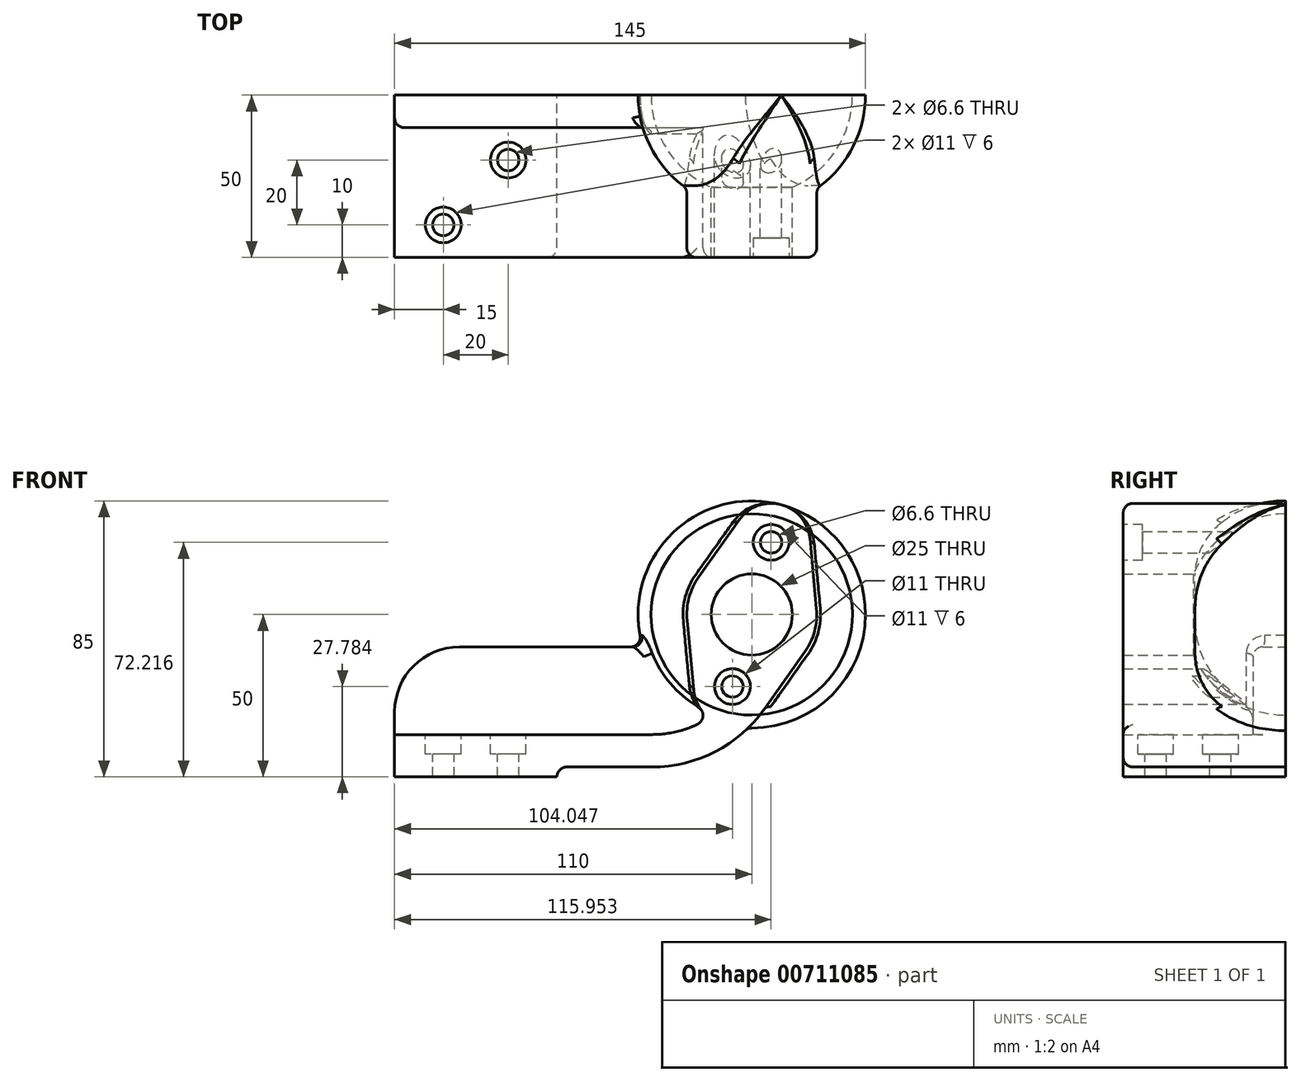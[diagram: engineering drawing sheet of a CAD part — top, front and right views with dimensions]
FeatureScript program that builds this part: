
annotation { "Feature Type Name" : "Feature", "Feature Type Description" : "" }
export const myFeature = defineFeature(function(context is Context, id is Id, definition is map)
    precondition{}
    {
        {
            var Q0;
            Q0=qCreatedBy(makeId("Front.planeOp"),FACE);
            var sketch = newSketch(context, id + "F0", { "sketchPlane" : qUnion([Q0])});
            skCircle(sketch, "E0", {"center": v(0, 0) * mm, "radius": 35 * mm});
            skLineSegment(sketch, "E1", {"start": v(-35, 0) * mm, "end": v(35, 0) * mm});
            skSolve(sketch);
        }
        {
            var Q0;
            {var subQ0=sQuery(id+"F0.wireOp",EDGE,"E1");Q0=makeQuery(id+"F0.imprint","IMPRINT",FACE,{"disambiguationData":[TD([[makeQuery(id+"F0.imprint","IMPRINT",EDGE,{"derivedFrom":subQ0}),1.0]])]});}
            var Q1;
            Q1=sQuery(id+"F0.wireOp",EDGE,"E1");
            revolve(context, id + "F1", {"surfaceOperationType" : NewSurfaceOperationType.NEW, "entities" : qUnion([Q0]), "axis" : qUnion([Q1]), "revolveType" : RevolveType.ONE_DIRECTION, "angle" : 180 * degree});
        }
        {
            var Q0;
            Q0=qCreatedBy(makeId("Front.planeOp"),FACE);
            var sketch = newSketch(context, id + "F2", { "sketchPlane" : qUnion([Q0])});
            skCircle(sketch, "E2.0", {"center": v(0, 0) * mm, "radius": 35 * mm});
            skLineSegment(sketch, "E3", {"start": v(-33.54, -10) * mm, "end": v(-110, -10) * mm});
            skLineSegment(sketch, "E4", {"start": v(-110, -10) * mm, "end": v(-110, -50) * mm});
            skLineSegment(sketch, "E5", {"start": v(-110, -50) * mm, "end": v(-60, -50) * mm});
            skLineSegment(sketch, "E6", {"start": v(-60, -50) * mm, "end": v(-60, -47) * mm});
            skLineSegment(sketch, "E7", {"start": v(-60, -47) * mm, "end": v(-30.7, -47) * mm});
            skArc(sketch, "E8", {"start": v(-30.7, -47) * mm, "mid": v(-11.26, -42.28) * mm, "end": v(3.83, -29.16) * mm});
            skLineSegment(sketch, "E9", {"start": v(-110, -37) * mm, "end": v(-30.7, -37) * mm});
            skArc(sketch, "E10", {"start": v(-30.7, -37) * mm, "mid": v(-21.55, -35.68) * mm, "end": v(-13.14, -31.82) * mm});
            skLineSegment(sketch, "E11", {"start": v(0, 35) * mm, "end": v(0, -35) * mm, "construction": true});
            skLineSegment(sketch, "E12", {"start": v(-35, 0) * mm, "end": v(35, 0) * mm, "construction": true});
            skLineSegment(sketch, "E13", {"start": v(9.06, 33.8) * mm, "end": v(-9.06, -33.8) * mm, "construction": true});
            skLineSegment(sketch, "E14", {"start": v(-33.8, 9.06) * mm, "end": v(33.8, -9.06) * mm, "construction": true});
            skCircle(sketch, "E15", {"center": v(0, 0) * mm, "radius": 12.5 * mm});
            skCircle(sketch, "E16", {"center": v(5.95, 22.22) * mm, "radius": 3.3 * mm});
            skCircle(sketch, "E17", {"center": v(5.95, 22.22) * mm, "radius": 5.5 * mm});
            skCircle(sketch, "E18.MirrorC", {"center": v(-5.95, -22.22) * mm, "radius": 5.5 * mm});
            skCircle(sketch, "E19.MirrorC", {"center": v(-5.95, -22.22) * mm, "radius": 3.3 * mm});
            skCircle(sketch, "E20", {"center": v(0, 0) * mm, "radius": 23 * mm, "construction": true});
            skArc(sketch, "E21", {"start": v(17.9, 23.34) * mm, "mid": v(15.12, 29.96) * mm, "end": v(9.06, 33.8) * mm});
            skArc(sketch, "E22", {"start": v(19.32, -5.18) * mm, "mid": v(19.93, -1.68) * mm, "end": v(19.91, 1.87) * mm});
            skLineSegment(sketch, "E23", {"start": v(17.9, 23.34) * mm, "end": v(19.91, 1.87) * mm});
            skArc(sketch, "E24.MirrorCS", {"start": v(-3.83, 29.16) * mm, "mid": v(1.88, 33.5) * mm, "end": v(9.06, 33.8) * mm});
            skLineSegment(sketch, "E25.MirrorCS", {"start": v(-3.83, 29.16) * mm, "end": v(-16.31, 11.57) * mm});
            skArc(sketch, "E26.MirrorCS", {"start": v(-19.32, 5.18) * mm, "mid": v(-18.1, 8.5) * mm, "end": v(-16.31, 11.57) * mm});
            skArc(sketch, "E27.MirrorCS", {"start": v(-19.32, 5.18) * mm, "mid": v(-19.93, 1.68) * mm, "end": v(-19.91, -1.87) * mm});
            skLineSegment(sketch, "E28.MirrorCS", {"start": v(-17.9, -23.34) * mm, "end": v(-19.91, -1.87) * mm});
            skArc(sketch, "E29.MirrorCS", {"start": v(-17.9, -23.34) * mm, "mid": v(-15.12, -29.96) * mm, "end": v(-9.06, -33.8) * mm});
            skLineSegment(sketch, "E30.MirrorCS", {"start": v(3.83, -29.16) * mm, "end": v(16.31, -11.57) * mm});
            skArc(sketch, "E31.MirrorCS", {"start": v(19.32, -5.18) * mm, "mid": v(18.1, -8.5) * mm, "end": v(16.31, -11.57) * mm});
            skArc(sketch, "E32", {"start": v(-9.06, -33.8) * mm, "mid": v(-1.88, -33.5) * mm, "end": v(3.83, -29.16) * mm});
            skLineSegment(sketch, "E33", {"start": v(-33.54, -10) * mm, "end": v(-13.14, -10) * mm});
            skLineSegment(sketch, "E34", {"start": v(-13.14, -10) * mm, "end": v(-13.14, -31.82) * mm});
            skSolve(sketch);
        }
        {
            var Q0;
            {var subQ0=sQuery(id+"F2.wireOp",EDGE,"E5");Q0=makeQuery(id+"F2.imprint","IMPRINT",FACE,{"disambiguationData":[TD([[makeQuery(id+"F2.imprint","IMPRINT",EDGE,{"derivedFrom":subQ0}),1.0]])]});}
            var Q1;
            Q1=makeQuery(id+"F2.imprint","IMPRINT",FACE,{"disambiguationData":[TD([[makeQuery(id+"F2.imprint","IMPRINT",EDGE,{"derivedFrom":sQuery(id+"F2.wireOp",EDGE,"E15")}),-1.0]])]});
            var Q2;
            Q2=makeQuery(id+"F2.imprint","IMPRINT",FACE,{"disambiguationData":[TD([[makeQuery(id+"F2.imprint","IMPRINT",EDGE,{"derivedFrom":sQuery(id+"F2.wireOp",EDGE,"E19.MirrorC")}),-1.0]])]});
            var Q3;
            Q3=makeQuery(id+"F2.imprint","IMPRINT",FACE,{"disambiguationData":[TD([[makeQuery(id+"F2.imprint","IMPRINT",EDGE,{"derivedFrom":sQuery(id+"F2.wireOp",EDGE,"E18.MirrorC")}),-1.0]])]});
            var Q4;
            Q4=makeQuery(id+"F2.imprint","IMPRINT",FACE,{"disambiguationData":[TD([[makeQuery(id+"F2.imprint","IMPRINT",EDGE,{"derivedFrom":sQuery(id+"F2.wireOp",EDGE,"E15")}),1.0]])]});
            var Q5;
            Q5=makeQuery(id+"F2.imprint","IMPRINT",FACE,{"disambiguationData":[TD([[makeQuery(id+"F2.imprint","IMPRINT",EDGE,{"derivedFrom":sQuery(id+"F2.wireOp",EDGE,"E16")}),-1.0]])]});
            var Q6;
            Q6=makeQuery(id+"F2.imprint","IMPRINT",FACE,{"disambiguationData":[TD([[makeQuery(id+"F2.imprint","IMPRINT",EDGE,{"derivedFrom":sQuery(id+"F2.wireOp",EDGE,"E16")}),1.0]])]});
            var Q7;
            {var subQ0=sQuery(id+"F2.wireOp",EDGE,"E32");Q7=makeQuery(id+"F2.imprint","IMPRINT",FACE,{"disambiguationData":[TD([[makeQuery(id+"F2.imprint","IMPRINT",EDGE,{"derivedFrom":subQ0}),-1.0]])]});}
            var Q8;
            {var subQ0=sQuery(id+"F2.wireOp",EDGE,"E29.MirrorCS");var subQ3=sQuery(id+"F2.wireOp",EDGE,"E10");var subQ5=makeQuery(id+"F2.imprint","INTERSECT",VERTEX,{"derivedFrom":[subQ3,subQ0]});Q8=makeQuery(id+"F2.imprint","IMPRINT",FACE,{"disambiguationData":[TD([[makeQuery(id+"F2.imprint","IMPRINT",EDGE,{"disambiguationData":[TD([[subQ5,1.0]])],"derivedFrom":subQ3}),-1.0]])]});}
            var Q9;
            {var subQ5=sQuery(id+"F2.wireOp",EDGE,"E34");Q9=makeQuery(id+"F2.imprint","IMPRINT",FACE,{"disambiguationData":[TD([[makeQuery(id+"F2.imprint","IMPRINT",EDGE,{"derivedFrom":subQ5}),-1.0]])]});}
            extrude(context, id + "F3", {"entities" : qUnion([Q0, Q1, Q2, Q3, Q4, Q5, Q6, Q7, Q8, Q9]), "operationType" : NewBodyOperationType.ADD, "depth" : 50 * mm, "offsetDistance" : 25 * mm});
        }
        {
            var Q0;
            {var subQ1=sQuery(id+"F2.wireOp",EDGE,"E3");Q0=makeQuery(id+"F2.imprint","IMPRINT",FACE,{"disambiguationData":[TD([[makeQuery(id+"F2.imprint","IMPRINT",EDGE,{"derivedFrom":subQ1}),1.0]])]});}
            var Q1;
            {var subQ0=sQuery(id+"F2.wireOp",EDGE,"E29.MirrorCS");var subQ1=sQuery(id+"F2.wireOp",EDGE,"E28.MirrorCS");var subQ2=makeQuery(id+"F2.imprint","INTERSECT",VERTEX,{"derivedFrom":[subQ1,subQ0]});Q1=makeQuery(id+"F2.imprint","IMPRINT",FACE,{"disambiguationData":[TD([[makeQuery(id+"F2.imprint","IMPRINT",EDGE,{"disambiguationData":[TD([[subQ2,-1.0]])],"derivedFrom":subQ1}),1.0]])]});}
            extrude(context, id + "F4", {"entities" : qUnion([Q0, Q1]), "operationType" : NewBodyOperationType.ADD, "depth" : 10 * mm, "offsetDistance" : 25 * mm});
        }
        {
            var Q0;
            Q0=makeQuery(id+"F2.imprint","IMPRINT",FACE,{"disambiguationData":[TD([[makeQuery(id+"F2.imprint","IMPRINT",EDGE,{"derivedFrom":sQuery(id+"F2.wireOp",EDGE,"E15")}),1.0]])]});
            var Q1;
            Q1=makeQuery(id+"F2.imprint","IMPRINT",FACE,{"disambiguationData":[TD([[makeQuery(id+"F2.imprint","IMPRINT",EDGE,{"derivedFrom":sQuery(id+"F2.wireOp",EDGE,"E16")}),1.0]])]});
            var Q2;
            Q2=makeQuery(id+"F2.imprint","IMPRINT",FACE,{"disambiguationData":[TD([[makeQuery(id+"F2.imprint","IMPRINT",EDGE,{"derivedFrom":sQuery(id+"F2.wireOp",EDGE,"E19.MirrorC")}),-1.0]])]});
            extrude(context, id + "F5", {"entities" : qUnion([Q0, Q1, Q2]), "operationType" : NewBodyOperationType.REMOVE, "endBound" : BoundingType.THROUGH_ALL, "depth" : 25 * mm, "offsetDistance" : 25 * mm});
        }
        {
            var Q0;
            Q0=makeQuery(id+"F3.opExtrude","CAP_FACE",FACE,{"disambiguationData":[OSD([sQuery(id+"F2.wireOp",EDGE,"E4"),sQuery(id+"F2.wireOp",EDGE,"E5"),sQuery(id+"F2.wireOp",EDGE,"E6"),sQuery(id+"F2.wireOp",EDGE,"E7"),sQuery(id+"F2.wireOp",EDGE,"E8"),sQuery(id+"F2.wireOp",EDGE,"E9"),sQuery(id+"F2.wireOp",EDGE,"E10"),sQuery(id+"F2.wireOp",EDGE,"E21"),sQuery(id+"F2.wireOp",EDGE,"E22"),sQuery(id+"F2.wireOp",EDGE,"E23"),sQuery(id+"F2.wireOp",EDGE,"E24.MirrorCS"),sQuery(id+"F2.wireOp",EDGE,"E25.MirrorCS"),sQuery(id+"F2.wireOp",EDGE,"E26.MirrorCS"),sQuery(id+"F2.wireOp",EDGE,"E27.MirrorCS"),sQuery(id+"F2.wireOp",EDGE,"E28.MirrorCS"),sQuery(id+"F2.wireOp",EDGE,"E29.MirrorCS"),sQuery(id+"F2.wireOp",EDGE,"E30.MirrorCS"),sQuery(id+"F2.wireOp",EDGE,"E31.MirrorCS")])],"isStart":false});
            var sketch = newSketch(context, id + "F6", { "sketchPlane" : qUnion([Q0])});
            skCircle(sketch, "E35.0", {"center": v(5.95, 22.22) * mm, "radius": 5.5 * mm});
            skCircle(sketch, "E36.0", {"center": v(-5.95, -22.22) * mm, "radius": 5.5 * mm});
            skSolve(sketch);
        }
        {
            var Q0;
            Q0 = qSketchRegion(id + "F6", true);
            extrude(context, id + "F7", {"entities" : qUnion([Q0]), "operationType" : NewBodyOperationType.REMOVE, "oppositeDirection" : true, "depth" : 6 * mm, "offsetDistance" : 25 * mm});
        }
        {
            var Q0;
            Q0=qCreatedBy(makeId("Front.planeOp"),FACE);
            var sketch = newSketch(context, id + "F8", { "sketchPlane" : qUnion([Q0])});
            skCircle(sketch, "E37.0", {"center": v(0, 0) * mm, "radius": 35 * mm});
            skCircle(sketch, "E38.0", {"center": v(0, 0) * mm, "radius": 31 * mm});
            skLineSegment(sketch, "E39", {"start": v(-31, 0) * mm, "end": v(31, 0) * mm});
            skSolve(sketch);
        }
        {
            var Q0;
            {var subQ0=sQuery(id+"F8.wireOp",EDGE,"E39");Q0=makeQuery(id+"F8.imprint","IMPRINT",FACE,{"disambiguationData":[TD([[makeQuery(id+"F8.imprint","IMPRINT",EDGE,{"derivedFrom":subQ0}),1.0]])]});}
            var Q1;
            Q1=sQuery(id+"F8.wireOp",EDGE,"E39");
            revolve(context, id + "F9", {"operationType" : NewBodyOperationType.REMOVE, "surfaceOperationType" : NewSurfaceOperationType.NEW, "entities" : qUnion([Q0]), "axis" : qUnion([Q1]), "revolveType" : RevolveType.FULL, "oppositeDirection" : true});
        }
        {
            var Q0;
            Q0=makeQuery(id+"F3.opExtrude","SWEPT_FACE",FACE,{"disambiguationData":[OSD([sQuery(id+"F2.wireOp",EDGE,"E9")])]});
            var sketch = newSketch(context, id + "F10", { "sketchPlane" : qUnion([Q0])});
            skCircle(sketch, "E40", {"center": v(-95, -40) * mm, "radius": 3.3 * mm});
            skCircle(sketch, "E41", {"center": v(-95, -40) * mm, "radius": 5.5 * mm});
            skCircle(sketch, "E42", {"center": v(-75, -20) * mm, "radius": 3.3 * mm});
            skCircle(sketch, "E43", {"center": v(-75, -20) * mm, "radius": 5.5 * mm});
            skSolve(sketch);
        }
        {
            var Q0;
            Q0=makeQuery(id+"F10.imprint","IMPRINT",FACE,{"disambiguationData":[TD([[makeQuery(id+"F10.imprint","IMPRINT",EDGE,{"derivedFrom":sQuery(id+"F10.wireOp",EDGE,"E42")}),1.0]])]});
            var Q1;
            Q1=makeQuery(id+"F10.imprint","IMPRINT",FACE,{"disambiguationData":[TD([[makeQuery(id+"F10.imprint","IMPRINT",EDGE,{"derivedFrom":sQuery(id+"F10.wireOp",EDGE,"E40")}),1.0]])]});
            extrude(context, id + "F11", {"entities" : qUnion([Q0, Q1]), "operationType" : NewBodyOperationType.REMOVE, "endBound" : BoundingType.THROUGH_ALL, "oppositeDirection" : true, "depth" : 25 * mm, "offsetDistance" : 25 * mm});
        }
        {
            var Q0;
            Q0=makeQuery(id+"F10.imprint","IMPRINT",FACE,{"disambiguationData":[TD([[makeQuery(id+"F10.imprint","IMPRINT",EDGE,{"derivedFrom":sQuery(id+"F10.wireOp",EDGE,"E42")}),-1.0]])]});
            var Q1;
            Q1=makeQuery(id+"F10.imprint","IMPRINT",FACE,{"disambiguationData":[TD([[makeQuery(id+"F10.imprint","IMPRINT",EDGE,{"derivedFrom":sQuery(id+"F10.wireOp",EDGE,"E40")}),-1.0]])]});
            extrude(context, id + "F12", {"entities" : qUnion([Q0, Q1]), "operationType" : NewBodyOperationType.REMOVE, "oppositeDirection" : true, "depth" : 6 * mm, "offsetDistance" : 25 * mm});
        }
        {
            var Q0;
            Q0=makeQuery(id+"F4.opExtrude","SWEPT_EDGE",EDGE,{"disambiguationData":[OSD([sQuery(id+"F2.wireOp",EDGE,"E3"),sQuery(id+"F2.wireOp",EDGE,"E4")])]});
            fillet(context, id + "F13", {"entities" : qUnion([Q0]), "radius" : 20 * mm, "tangentPropagation" : true, "allowEdgeOverflow" : false});
        }
        {
            var Q0;
            Q0=makeQuery(id+"F4.opExtrude","CAP_EDGE",EDGE,{"disambiguationData":[OSD([sQuery(id+"F2.wireOp",EDGE,"E10")])],"isStart":false});
            var Q1;
            Q1=makeQuery(id+"F4.opExtrude","CAP_EDGE",EDGE,{"disambiguationData":[OSD([sQuery(id+"F2.wireOp",EDGE,"E29.MirrorCS")])],"isStart":false});
            var Q2;
            {var subQ0=sQuery(id+"F2.wireOp",EDGE,"E29.MirrorCS");var subQ1=sQuery(id+"F2.wireOp",EDGE,"E28.MirrorCS");var subQ2=sQuery(id+"F2.wireOp",EDGE,"E10");var subQ3=sQuery(id+"F2.wireOp",EDGE,"E9");var subQ4=sQuery(id+"F2.wireOp",EDGE,"E4");var subQ10=sQuery(id+"F0.wireOp",EDGE,"E0");var subQ11=makeQuery(id+"F1.opRevolve","SWEPT_FACE",FACE,{"disambiguationData":[OSD([subQ10])]});Q2=makeQuery(id+"F4.boolean.opBoolean","INTERSECT",EDGE,{"derivedFrom":[makeQuery(id+"F3.boolean.opBoolean","SPLIT",FACE,{"disambiguationData":[TD([makeQuery(id+"F3.opExtrude","SWEPT_FACE",FACE,{"disambiguationData":[OSD([subQ2])]})])],"derivedFrom":subQ11}),makeQuery(id+"F4.opExtrude","CAP_FACE",FACE,{"disambiguationData":[OSD([sQuery(id+"F2.wireOp",EDGE,"E3"),subQ4,subQ3,subQ2,subQ1,subQ0,sQuery(id+"F2.wireOp",EDGE,"E33")])],"isStart":false})]});}
            var Q3;
            Q3=makeQuery(id+"F3.boolean.opBoolean","INTERSECT",EDGE,{"derivedFrom":[makeQuery(id+"F1.opRevolve","SWEPT_FACE",FACE,{"disambiguationData":[OSD([sQuery(id+"F0.wireOp",EDGE,"E0")])]}),makeQuery(id+"F3.opExtrude","SWEPT_FACE",FACE,{"disambiguationData":[OSD([sQuery(id+"F2.wireOp",EDGE,"E29.MirrorCS")])]})]});
            var Q4;
            Q4=makeQuery(id+"F3.opExtrude","SWEPT_EDGE",EDGE,{"disambiguationData":[OSD([sQuery(id+"F2.wireOp",EDGE,"E10"),sQuery(id+"F2.wireOp",EDGE,"E29.MirrorCS"),sQuery(id+"F2.wireOp",EDGE,"E34")])]});
            var Q5;
            {var subQ7=sQuery(id+"F2.wireOp",EDGE,"E10");var subQ8=sQuery(id+"F0.wireOp",EDGE,"E0");var subQ9=makeQuery(id+"F1.opRevolve","SWEPT_FACE",FACE,{"disambiguationData":[OSD([subQ8])]});Q5=makeQuery(id+"F4.boolean.opBoolean","INTERSECT",EDGE,{"derivedFrom":[makeQuery(id+"F3.boolean.opBoolean","SPLIT",FACE,{"disambiguationData":[TD([makeQuery(id+"F3.opExtrude","SWEPT_FACE",FACE,{"disambiguationData":[OSD([subQ7])]})])],"derivedFrom":subQ9}),makeQuery(id+"F4.opExtrude","SWEPT_FACE",FACE,{"disambiguationData":[OSD([sQuery(id+"F2.wireOp",EDGE,"E3"),sQuery(id+"F2.wireOp",EDGE,"E33")])]})]});}
            var Q6;
            Q6=makeQuery(id+"F4.opExtrude","CAP_EDGE",EDGE,{"disambiguationData":[OSD([sQuery(id+"F2.wireOp",EDGE,"E3"),sQuery(id+"F2.wireOp",EDGE,"E33")])],"isStart":false});
            var Q7;
            Q7=makeQuery(id+"F3.opExtrude","SWEPT_EDGE",EDGE,{"disambiguationData":[OSD([sQuery(id+"F2.wireOp",EDGE,"E6"),sQuery(id+"F2.wireOp",EDGE,"E7")])]});
            var Q8;
            Q8=makeQuery(id+"F3.opExtrude","CAP_EDGE",EDGE,{"disambiguationData":[OSD([sQuery(id+"F2.wireOp",EDGE,"E7")])],"isStart":false});
            var Q9;
            Q9=makeQuery(id+"F3.boolean.opBoolean","INTERSECT",EDGE,{"derivedFrom":[makeQuery(id+"F1.opRevolve","SWEPT_FACE",FACE,{"disambiguationData":[OSD([sQuery(id+"F0.wireOp",EDGE,"E0")])]}),makeQuery(id+"F3.opExtrude","SWEPT_FACE",FACE,{"disambiguationData":[OSD([sQuery(id+"F2.wireOp",EDGE,"E23")])]})]});
            fillet(context, id + "F14", {"entities" : qUnion([Q0, Q1, Q2, Q3, Q4, Q5, Q6, Q7, Q8, Q9]), "radius" : 3 * mm, "tangentPropagation" : true, "allowEdgeOverflow" : false});
        }
    });
